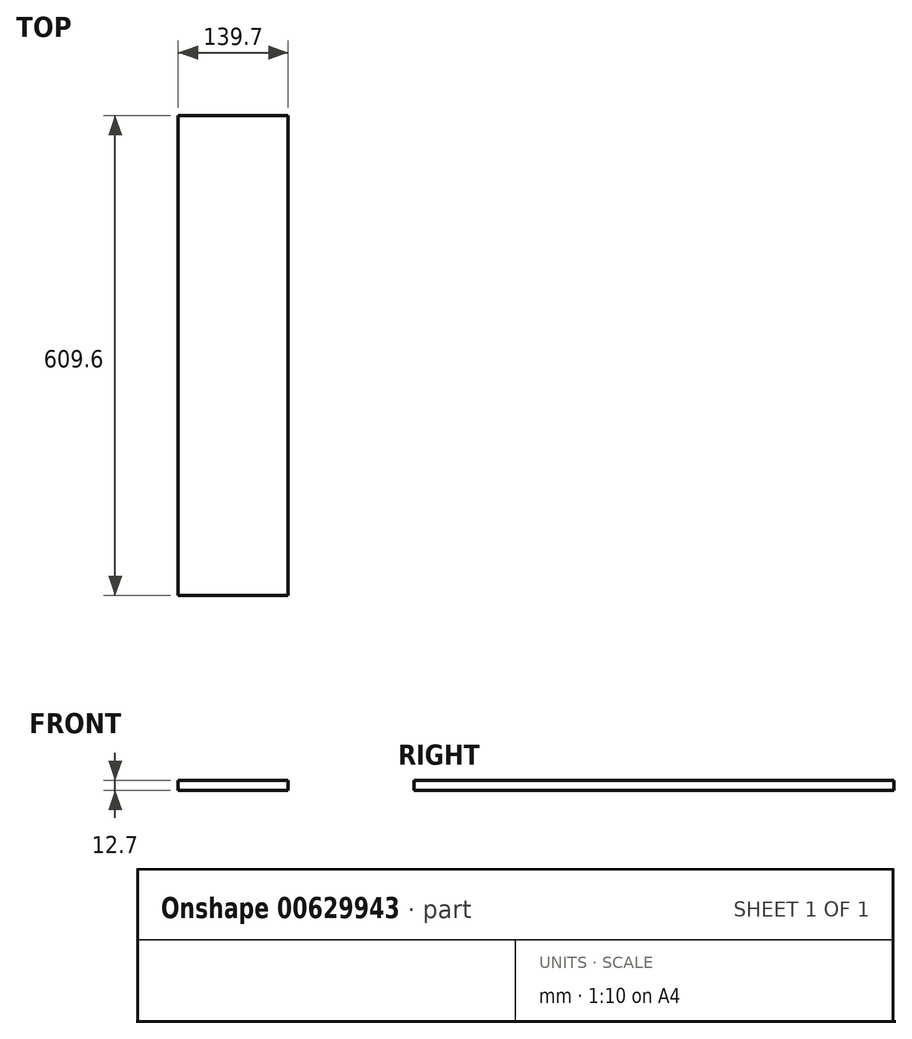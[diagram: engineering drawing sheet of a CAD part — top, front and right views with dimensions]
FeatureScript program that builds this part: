
annotation { "Feature Type Name" : "Feature", "Feature Type Description" : "" }
export const myFeature = defineFeature(function(context is Context, id is Id, definition is map)
    precondition{}
    {
        {
            var Q0;
            Q0=qCreatedBy(makeId("Front.planeOp"),FACE);
            var sketch = newSketch(context, id + "F0", { "sketchPlane" : qUnion([Q0])});
            skLineSegment(sketch, "E0.bottom", {"start": v(-78.52, 12.7) * mm, "end": v(61.18, 12.7) * mm});
            skLineSegment(sketch, "E0.top", {"start": v(-78.52, 0) * mm, "end": v(61.18, 0) * mm});
            skLineSegment(sketch, "E0.left", {"start": v(-78.52, 12.7) * mm, "end": v(-78.52, 0) * mm});
            skLineSegment(sketch, "E0.right", {"start": v(61.18, 12.7) * mm, "end": v(61.18, 0) * mm});
            skSolve(sketch);
        }
        {
            var Q0;
            Q0 = qSketchRegion(id + "F0", true);
            extrude(context, id + "F1", {"entities" : qUnion([Q0]), "depth" : 609.6 * mm, "offsetDistance" : 25.4 * mm});
        }
    });
